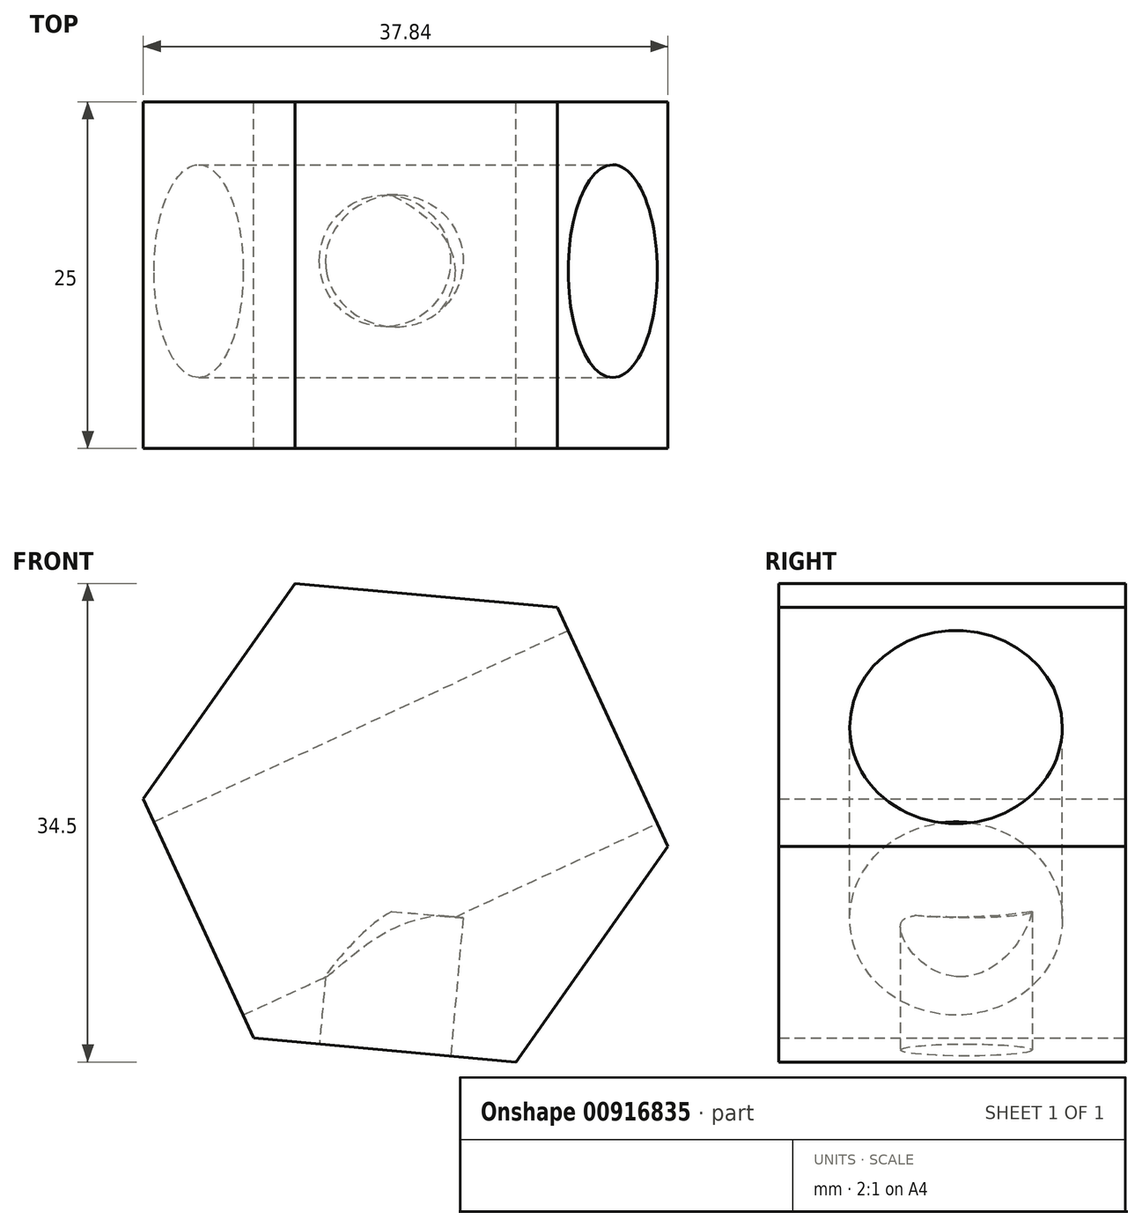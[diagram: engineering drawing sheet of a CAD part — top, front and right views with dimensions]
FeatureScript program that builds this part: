
annotation { "Feature Type Name" : "Feature", "Feature Type Description" : "" }
export const myFeature = defineFeature(function(context is Context, id is Id, definition is map)
    precondition{}
    {
        {
            var Q0;
            Q0=qCreatedBy(makeId("Front.planeOp"),FACE);
            var sketch = newSketch(context, id + "F0", { "sketchPlane" : qUnion([Q0])});
            skCircle(sketch, "E0.cCircle", {"center": v(0, 0) * mm, "radius": 16.45 * mm, "construction": true});
            skLineSegment(sketch, "E0.0", {"start": v(-18.92, 1.72) * mm, "end": v(-7.97, 17.25) * mm});
            skLineSegment(sketch, "E0.1", {"start": v(-7.97, 17.25) * mm, "end": v(10.95, 15.53) * mm});
            skLineSegment(sketch, "E0.2", {"start": v(10.95, 15.53) * mm, "end": v(18.92, -1.72) * mm});
            skLineSegment(sketch, "E0.3", {"start": v(18.92, -1.72) * mm, "end": v(7.97, -17.25) * mm});
            skLineSegment(sketch, "E0.4", {"start": v(7.97, -17.25) * mm, "end": v(-10.95, -15.53) * mm});
            skLineSegment(sketch, "E0.5", {"start": v(-10.95, -15.53) * mm, "end": v(-18.92, 1.72) * mm});
            skPoint(sketch, "E0.0.midPoint", {"position": v(-13.45, 9.48) * mm});
            skSolve(sketch);
        }
        {
            var Q0;
            Q0=makeQuery(id+"F0.imprint","IMPRINT",FACE,{"disambiguationData":[TD([[makeQuery(id+"F0.imprint","IMPRINT",EDGE,{"derivedFrom":sQuery(id+"F0.wireOp",EDGE,"E0.0")}),-1.0]])]});
            extrude(context, id + "F1", {"entities" : qUnion([Q0]), "depth" : 25 * mm, "offsetDistance" : 25 * mm});
        }
        {
            var Q0;
            Q0=makeQuery(id+"F1.opExtrude","SWEPT_FACE",FACE,{"disambiguationData":[OSD([sQuery(id+"F0.wireOp",EDGE,"E0.4")])]});
            var sketch = newSketch(context, id + "F2", { "sketchPlane" : qUnion([Q0])});
            skCircle(sketch, "E1", {"center": v(0, 11.48) * mm, "radius": 4.75 * mm});
            skSolve(sketch);
        }
        {
            var Q0;
            Q0 = qSketchRegion(id + "F2", true);
            extrude(context, id + "F3", {"entities" : qUnion([Q0]), "operationType" : NewBodyOperationType.REMOVE, "oppositeDirection" : true, "depth" : 10 * mm, "offsetDistance" : 25 * mm});
        }
        {
            var Q0;
            Q0=makeQuery(id+"F1.opExtrude","SWEPT_FACE",FACE,{"disambiguationData":[OSD([sQuery(id+"F0.wireOp",EDGE,"E0.2")])]});
            var sketch = newSketch(context, id + "F4", { "sketchPlane" : qUnion([Q0])});
            skCircle(sketch, "E2", {"center": v(-12.21, 0) * mm, "radius": 7.67 * mm});
            skSolve(sketch);
        }
        {
            var Q0;
            Q0=makeQuery(id+"F4.imprint","IMPRINT",FACE,{"disambiguationData":[TD([[makeQuery(id+"F4.imprint","IMPRINT",EDGE,{"derivedFrom":sQuery(id+"F4.wireOp",EDGE,"E2")}),1.0]])]});
            extrude(context, id + "F5", {"entities" : qUnion([Q0]), "operationType" : NewBodyOperationType.REMOVE, "oppositeDirection" : true, "depth" : 39.4 * mm, "offsetDistance" : 25 * mm});
        }
    });
